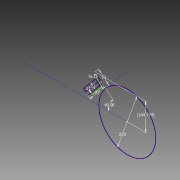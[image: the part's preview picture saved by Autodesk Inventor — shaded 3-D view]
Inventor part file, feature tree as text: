
AUTODESK INVENTOR PART (.ipt)
format: ipt  version: 2015 (Build 190159000, 159)  size: 72,704 bytes
history: native  units: mm
features: sketch x1
ambient origin geometry x8: Origin, YZ Plane, XZ Plane, XY Plane, X Axis, Y Axis, Z Axis, Center Point
feature tree (1):
  sketch  "Sketch1"  dims[d0=220.0mm d1=53.0mm d2=87.0mm d3=6.981317mm d4=104.77438mm d5=11.0mm d6=22.0mm d8=15.0mm]
